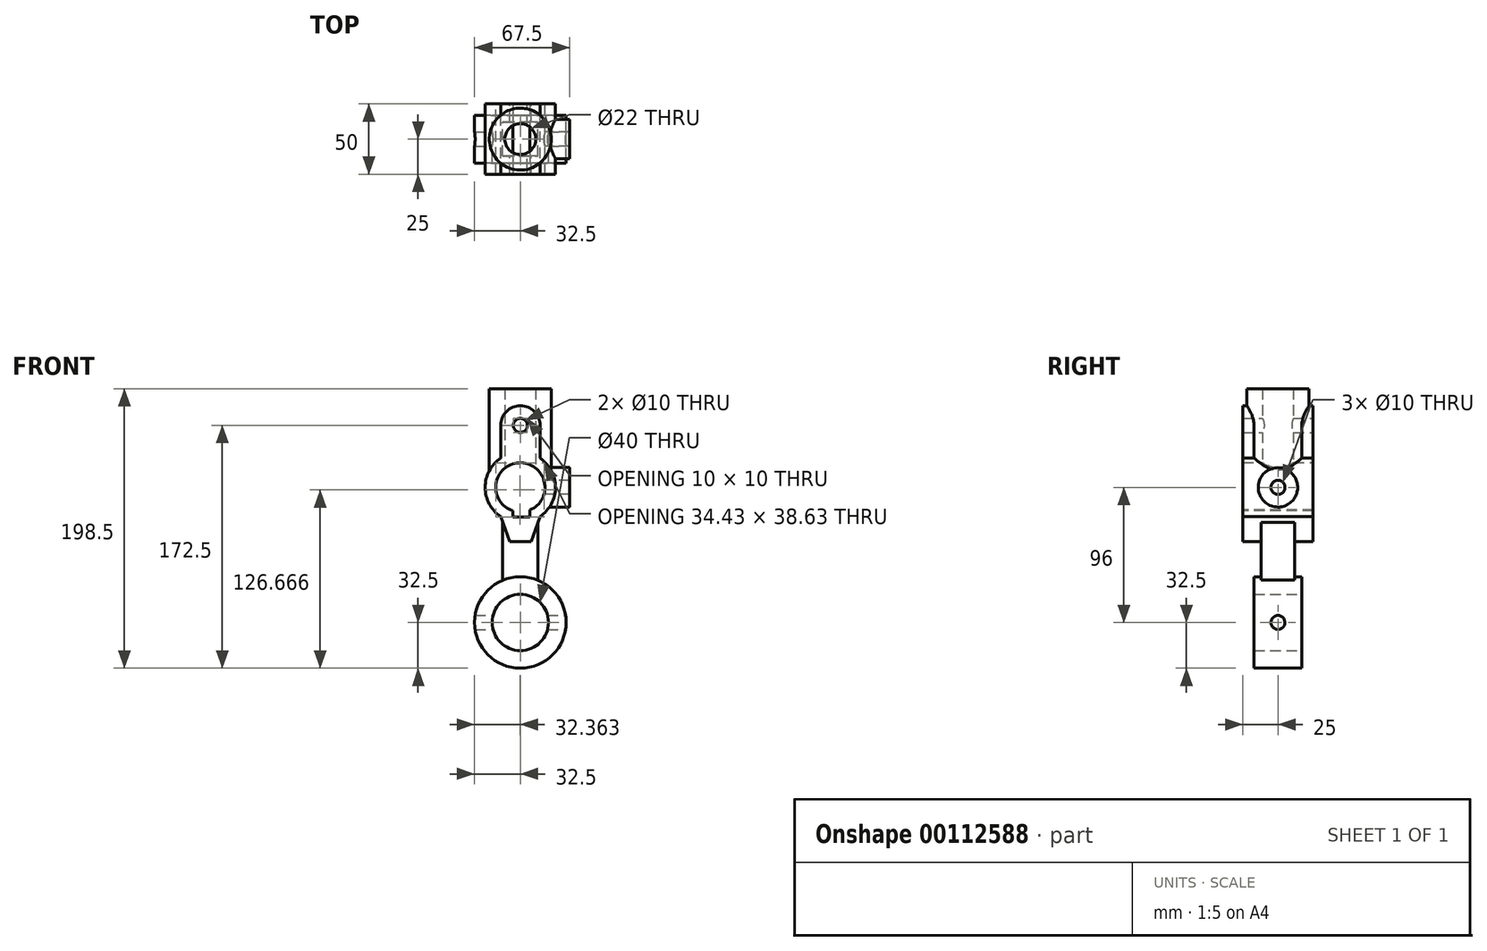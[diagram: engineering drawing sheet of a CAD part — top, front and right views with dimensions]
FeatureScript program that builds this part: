
annotation { "Feature Type Name" : "Feature", "Feature Type Description" : "" }
export const myFeature = defineFeature(function(context is Context, id is Id, definition is map)
    precondition{}
    {
        {
            var Q0;
            Q0=qCreatedBy(makeId("Front.planeOp"),FACE);
            var sketch = newSketch(context, id + "F0", { "sketchPlane" : qUnion([Q0])});
            skCircle(sketch, "E0", {"center": v(0, 0) * mm, "radius": 20 * mm});
            skCircle(sketch, "E1", {"center": v(0, 0) * mm, "radius": 32.5 * mm});
            skSolve(sketch);
        }
        {
            var Q0;
            Q0 = qSketchRegion(id + "F0", true);
            extrude(context, id + "F1", {"entities" : qUnion([Q0]), "endBound" : BoundingType.SYMMETRIC, "depth" : 34 * mm});
        }
        {
            var Q0;
            Q0=qCreatedBy(makeId("Front.planeOp"),FACE);
            var sketch = newSketch(context, id + "F2", { "sketchPlane" : qUnion([Q0])});
            skLineSegment(sketch, "E2", {"start": v(0, 0) * mm, "end": v(0, 96) * mm, "construction": true});
            skCircle(sketch, "E3", {"center": v(0, 96) * mm, "radius": 17.5 * mm});
            skLineSegment(sketch, "E4", {"start": v(0, 96) * mm, "end": v(0, 140) * mm, "construction": true});
            skCircle(sketch, "E5", {"center": v(0, 140) * mm, "radius": 5 * mm});
            skArc(sketch, "E6", {"start": v(14, 140) * mm, "mid": v(0, 154) * mm, "end": v(-14, 140) * mm});
            skArc(sketch, "E7", {"start": v(14, 75.29) * mm, "mid": v(25, 96) * mm, "end": v(14, 116.71) * mm});
            skArc(sketch, "E8", {"start": v(-14, 116.71) * mm, "mid": v(-25, 96) * mm, "end": v(-14, 75.29) * mm});
            skLineSegment(sketch, "E9", {"start": v(-14, 116.71) * mm, "end": v(-14, 140) * mm});
            skLineSegment(sketch, "E10", {"start": v(14, 116.71) * mm, "end": v(14, 140) * mm});
            skLineSegment(sketch, "E11", {"start": v(14, 116.71) * mm, "end": v(14, -52.44) * mm, "construction": true});
            skLineSegment(sketch, "E12", {"start": v(-14, 116.71) * mm, "end": v(-14, -49.57) * mm, "construction": true});
            skLineSegment(sketch, "E13", {"start": v(-14, 75.29) * mm, "end": v(-7.6, 57.48) * mm});
            skLineSegment(sketch, "E14", {"start": v(-7.6, 57.48) * mm, "end": v(7.6, 57.48) * mm});
            skLineSegment(sketch, "E15", {"start": v(7.6, 57.48) * mm, "end": v(14, 75.29) * mm});
            skSolve(sketch);
        }
        {
            var Q0;
            Q0 = qSketchRegion(id + "F2", true);
            extrude(context, id + "F3", {"entities" : qUnion([Q0]), "operationType" : NewBodyOperationType.ADD, "endBound" : BoundingType.SYMMETRIC, "depth" : 50 * mm});
        }
        {
            var Q0;
            Q0=qCreatedBy(makeId("Right.planeOp"),FACE);
            var sketch = newSketch(context, id + "F4", { "sketchPlane" : qUnion([Q0])});
            skLineSegment(sketch, "E16.0", {"start": v(-25, 75.29) * mm, "end": v(25, 75.29) * mm});
            skLineSegment(sketch, "E17", {"start": v(12, 75.29) * mm, "end": v(12, 23.1) * mm});
            skLineSegment(sketch, "E18", {"start": v(-12, 75.29) * mm, "end": v(-12, 23.1) * mm});
            skLineSegment(sketch, "E19", {"start": v(12, 23.1) * mm, "end": v(-12, 23.1) * mm});
            skLineSegment(sketch, "E20", {"start": v(12, 75.29) * mm, "end": v(-12, 75.29) * mm});
            skLineSegment(sketch, "E21", {"start": v(25, 75.29) * mm, "end": v(12, 75.29) * mm, "construction": true});
            skLineSegment(sketch, "E22", {"start": v(-12, 75.29) * mm, "end": v(-25, 75.29) * mm, "construction": true});
            skSolve(sketch);
        }
        {
            var Q0;
            Q0 = qSketchRegion(id + "F4", true);
            extrude(context, id + "F5", {"entities" : qUnion([Q0]), "operationType" : NewBodyOperationType.ADD, "endBound" : BoundingType.SYMMETRIC, "depth" : 25 * mm});
        }
        {
            var Q0;
            Q0=qCreatedBy(makeId("Top.planeOp"),FACE);
            var sketch = newSketch(context, id + "F6", { "sketchPlane" : qUnion([Q0])});
            skCircle(sketch, "E23", {"center": v(0, 0) * mm, "radius": 11 * mm});
            skCircle(sketch, "E24", {"center": v(0, 0) * mm, "radius": 22 * mm});
            skSolve(sketch);
        }
        {
            var Q0;
            Q0 = qSketchRegion(id + "F6", true);
            extrude(context, id + "F7", {"entities" : qUnion([Q0]), "operationType" : NewBodyOperationType.ADD, "depth" : 166 * mm, "hasSecondDirection" : true, "secondDirectionOppositeDirection" : false, "secondDirectionDepth" : 96 * mm});
        }
        {
            var Q0;
            Q0=qCreatedBy(makeId("Front.planeOp"),FACE);
            var sketch = newSketch(context, id + "F8", { "sketchPlane" : qUnion([Q0])});
            skCircle(sketch, "E25.0", {"center": v(0, 96) * mm, "radius": 17.5 * mm});
            skCircle(sketch, "E26.0", {"center": v(0, 140) * mm, "radius": 5 * mm});
            skLineSegment(sketch, "E27.bottom", {"start": v(-5.26, 79.85) * mm, "end": v(6.74, 79.85) * mm});
            skLineSegment(sketch, "E27.top", {"start": v(-5.26, 74.85) * mm, "end": v(6.74, 74.85) * mm});
            skLineSegment(sketch, "E27.left", {"start": v(-5.26, 79.85) * mm, "end": v(-5.26, 74.85) * mm});
            skLineSegment(sketch, "E27.right", {"start": v(6.74, 79.85) * mm, "end": v(6.74, 74.85) * mm});
            skSolve(sketch);
        }
        {
            var Q0;
            Q0 = qSketchRegion(id + "F8", true);
            extrude(context, id + "F9", {"entities" : qUnion([Q0]), "operationType" : NewBodyOperationType.REMOVE, "endBound" : BoundingType.SYMMETRIC, "oppositeDirection" : true, "depth" : 50 * mm});
        }
        {
            var Q0;
            Q0=qCreatedBy(makeId("Right.planeOp"),FACE);
            var sketch = newSketch(context, id + "F10", { "sketchPlane" : qUnion([Q0])});
            skLineSegment(sketch, "E28", {"start": v(0, 0) * mm, "end": v(0, 96) * mm, "construction": true});
            skCircle(sketch, "E29", {"center": v(0, 96) * mm, "radius": 14 * mm});
            skCircle(sketch, "E30", {"center": v(0, 96) * mm, "radius": 5 * mm});
            skSolve(sketch);
        }
        {
            var Q0;
            Q0 = qSketchRegion(id + "F10", true);
            extrude(context, id + "F11", {"entities" : qUnion([Q0]), "operationType" : NewBodyOperationType.ADD, "depth" : 35 * mm, "hasSecondDirection" : true, "secondDirectionOppositeDirection" : false, "secondDirectionDepth" : 18 * mm});
        }
        {
            var Q0;
            Q0=qCreatedBy(makeId("Right.planeOp"),FACE);
            var sketch = newSketch(context, id + "F12", { "sketchPlane" : qUnion([Q0])});
            skCircle(sketch, "E31", {"center": v(0, 0) * mm, "radius": 5 * mm});
            skSolve(sketch);
        }
        {
            var Q0;
            Q0 = qSketchRegion(id + "F12", true);
            extrude(context, id + "F13", {"entities" : qUnion([Q0]), "operationType" : NewBodyOperationType.REMOVE, "endBound" : BoundingType.SYMMETRIC, "oppositeDirection" : true, "depth" : 100 * mm});
        }
        {
            var Q0;
            Q0=qCreatedBy(makeId("Right.planeOp"),FACE);
            var sketch = newSketch(context, id + "F14", { "sketchPlane" : qUnion([Q0])});
            skCircle(sketch, "E32.0", {"center": v(0, 96) * mm, "radius": 5 * mm});
            skSolve(sketch);
        }
        {
            var Q0;
            Q0 = qSketchRegion(id + "F14", true);
            extrude(context, id + "F15", {"entities" : qUnion([Q0]), "operationType" : NewBodyOperationType.REMOVE, "depth" : 100 * mm});
        }
        {
            var Q0;
            Q0=qCreatedBy(makeId("Top.planeOp"),FACE);
            var sketch = newSketch(context, id + "F16", { "sketchPlane" : qUnion([Q0])});
            skCircle(sketch, "E33.0", {"center": v(0, 0) * mm, "radius": 11 * mm});
            skSolve(sketch);
        }
        {
            var Q0;
            Q0 = qSketchRegion(id + "F16", true);
            extrude(context, id + "F17", {"entities" : qUnion([Q0]), "operationType" : NewBodyOperationType.REMOVE, "depth" : 195.95 * mm, "hasSecondDirection" : true, "secondDirectionOppositeDirection" : false, "secondDirectionDepth" : 100.46 * mm});
        }
    });
